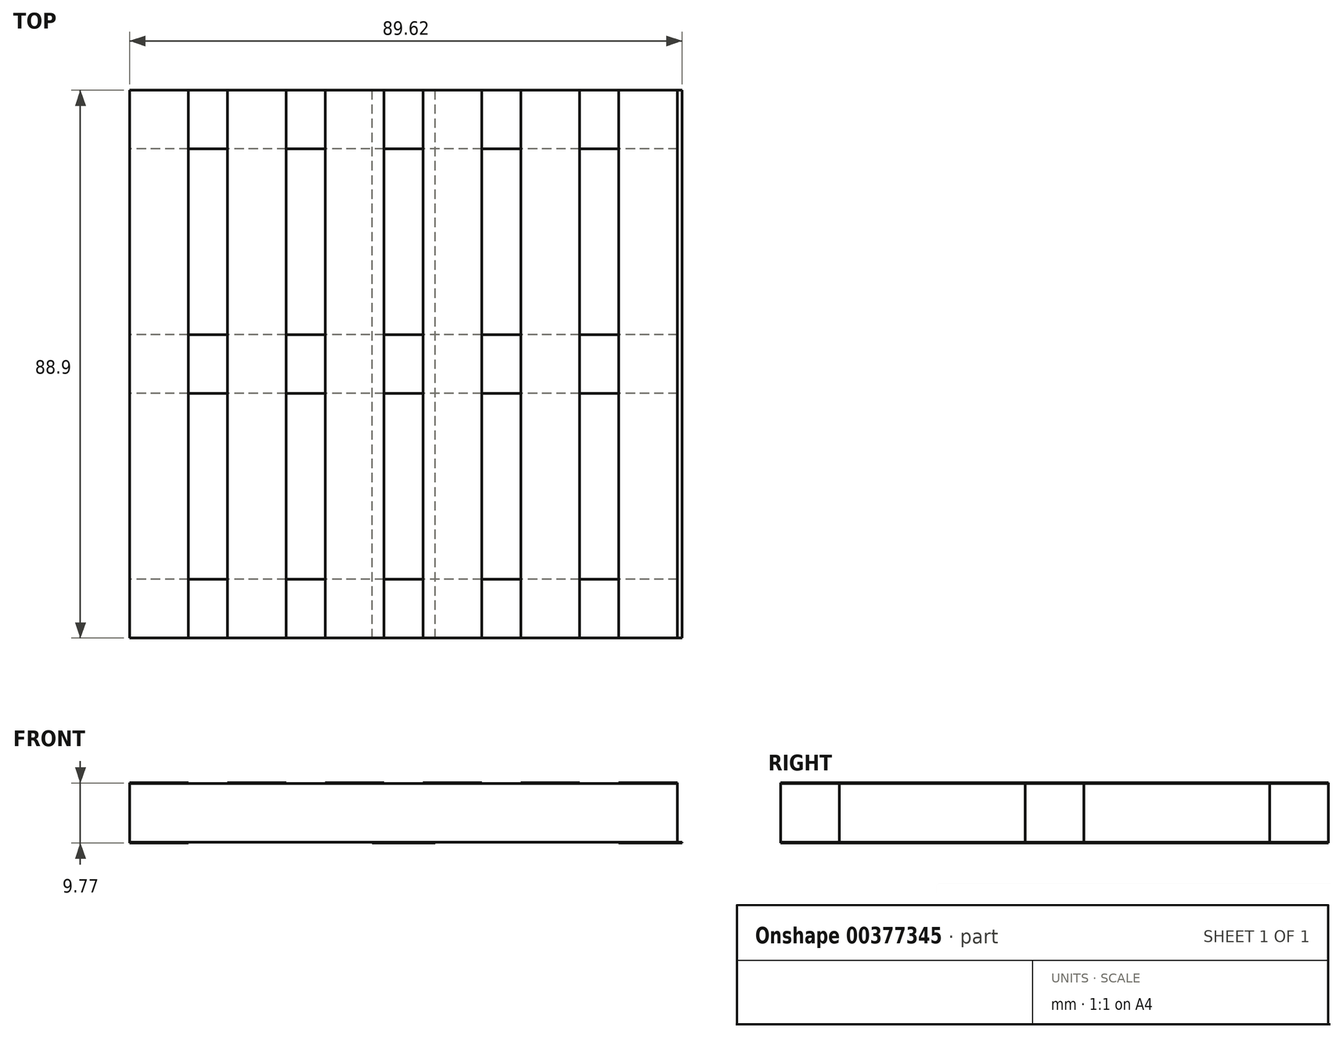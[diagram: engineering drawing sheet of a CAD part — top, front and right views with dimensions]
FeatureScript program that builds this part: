
annotation { "Feature Type Name" : "Feature", "Feature Type Description" : "" }
export const myFeature = defineFeature(function(context is Context, id is Id, definition is map)
    precondition{}
    {
        {
            assignVariable(context, id + "F0", {"name" : "slat_thickness", "anyValue" : 1 / 8});
        }
        {
            var Q0;
            Q0=qCreatedBy(makeId("Top.planeOp"),FACE);
            var sketch = newSketch(context, id + "F1", { "sketchPlane" : qUnion([Q0])});
            skLineSegment(sketch, "E0.bottom", {"start": v(44.45, -44.45) * mm, "end": v(-44.45, -44.45) * mm, "construction": true});
            skLineSegment(sketch, "E0.top", {"start": v(44.45, 44.45) * mm, "end": v(-44.45, 44.45) * mm, "construction": true});
            skLineSegment(sketch, "E0.left", {"start": v(44.45, -44.45) * mm, "end": v(44.45, 44.45) * mm, "construction": true});
            skLineSegment(sketch, "E0.right", {"start": v(-44.45, -44.45) * mm, "end": v(-44.45, 44.45) * mm, "construction": true});
            skPoint(sketch, "E0.middle", {"position": v(0, 0) * mm});
            skLineSegment(sketch, "E1.bottom", {"start": v(-44.45, -44.45) * mm, "end": v(-34.92, -44.45) * mm});
            skLineSegment(sketch, "E1.top", {"start": v(-44.45, 44.45) * mm, "end": v(-34.93, 44.45) * mm});
            skLineSegment(sketch, "E1.left", {"start": v(-44.45, -44.45) * mm, "end": v(-44.45, 44.45) * mm});
            skLineSegment(sketch, "E1.right", {"start": v(-34.92, -44.45) * mm, "end": v(-34.93, 44.45) * mm});
            skLineSegment(sketch, "E2.1.0.0", {"start": v(-19.05, -44.45) * mm, "end": v(-19.05, 44.45) * mm});
            skLineSegment(sketch, "E2.1.0.1", {"start": v(-28.57, -44.45) * mm, "end": v(-28.58, 44.45) * mm});
            skLineSegment(sketch, "E2.1.0.2", {"start": v(-28.58, 44.45) * mm, "end": v(-19.05, 44.45) * mm});
            skLineSegment(sketch, "E2.1.0.3", {"start": v(-28.57, -44.45) * mm, "end": v(-19.05, -44.45) * mm});
            skLineSegment(sketch, "E2.1.0.4", {"start": v(-28.57, -44.45) * mm, "end": v(-28.58, 44.45) * mm, "construction": true});
            skLineSegment(sketch, "E2.2.0.0", {"start": v(-3.17, -44.45) * mm, "end": v(-3.18, 44.45) * mm});
            skLineSegment(sketch, "E2.2.0.1", {"start": v(-12.7, -44.45) * mm, "end": v(-12.7, 44.45) * mm});
            skLineSegment(sketch, "E2.2.0.2", {"start": v(-12.7, 44.45) * mm, "end": v(-3.18, 44.45) * mm});
            skLineSegment(sketch, "E2.2.0.3", {"start": v(-12.7, -44.45) * mm, "end": v(-3.17, -44.45) * mm});
            skLineSegment(sketch, "E2.2.0.4", {"start": v(-12.7, -44.45) * mm, "end": v(-12.7, 44.45) * mm, "construction": true});
            skLineSegment(sketch, "E2.3.0.0", {"start": v(12.7, -44.45) * mm, "end": v(12.7, 44.45) * mm});
            skLineSegment(sketch, "E2.3.0.1", {"start": v(3.18, -44.45) * mm, "end": v(3.17, 44.45) * mm});
            skLineSegment(sketch, "E2.3.0.2", {"start": v(3.17, 44.45) * mm, "end": v(12.7, 44.45) * mm});
            skLineSegment(sketch, "E2.3.0.3", {"start": v(3.18, -44.45) * mm, "end": v(12.7, -44.45) * mm});
            skLineSegment(sketch, "E2.3.0.4", {"start": v(3.18, -44.45) * mm, "end": v(3.17, 44.45) * mm, "construction": true});
            skLineSegment(sketch, "E2.4.0.0", {"start": v(28.58, -44.45) * mm, "end": v(28.57, 44.45) * mm});
            skLineSegment(sketch, "E2.4.0.1", {"start": v(19.05, -44.45) * mm, "end": v(19.05, 44.45) * mm});
            skLineSegment(sketch, "E2.4.0.2", {"start": v(19.05, 44.45) * mm, "end": v(28.57, 44.45) * mm});
            skLineSegment(sketch, "E2.4.0.3", {"start": v(19.05, -44.45) * mm, "end": v(28.58, -44.45) * mm});
            skLineSegment(sketch, "E2.4.0.4", {"start": v(19.05, -44.45) * mm, "end": v(19.05, 44.45) * mm, "construction": true});
            skLineSegment(sketch, "E2.5.0.0", {"start": v(44.45, -44.45) * mm, "end": v(44.45, 44.45) * mm});
            skLineSegment(sketch, "E2.5.0.1", {"start": v(34.93, -44.45) * mm, "end": v(34.92, 44.45) * mm});
            skLineSegment(sketch, "E2.5.0.2", {"start": v(34.92, 44.45) * mm, "end": v(44.45, 44.45) * mm});
            skLineSegment(sketch, "E2.5.0.3", {"start": v(34.93, -44.45) * mm, "end": v(44.45, -44.45) * mm});
            skLineSegment(sketch, "E2.5.0.4", {"start": v(34.93, -44.45) * mm, "end": v(34.92, 44.45) * mm, "construction": true});
            skLineSegment(sketch, "E2.direction1", {"start": v(-44.45, -44.45) * mm, "end": v(-28.57, -44.45) * mm, "construction": true});
            skSolve(sketch);
        }
        {
            var Q0;
            Q0 = qSketchRegion(id + "F1", true);
            extrude(context, id + "F2", {"entities" : qUnion([Q0]), "depth" : (getVariable(context, 'slat_thickness')) * mm});
        }
        {
            var Q0;
            Q0=qCreatedBy(makeId("Right.planeOp"),FACE);
            var sketch = newSketch(context, id + "F3", { "sketchPlane" : qUnion([Q0])});
            skLineSegment(sketch, "E3.bottom", {"start": v(-44.45, 0) * mm, "end": v(-34.92, 0) * mm});
            skLineSegment(sketch, "E3.top", {"start": v(-44.45, -9.52) * mm, "end": v(-34.92, -9.52) * mm});
            skLineSegment(sketch, "E3.left", {"start": v(-44.45, 0) * mm, "end": v(-44.45, -9.53) * mm});
            skLineSegment(sketch, "E3.right", {"start": v(-34.92, 0) * mm, "end": v(-34.92, -9.53) * mm});
            skLineSegment(sketch, "E4.bottom", {"start": v(44.45, 0) * mm, "end": v(34.93, 0) * mm});
            skLineSegment(sketch, "E4.top", {"start": v(44.45, -9.52) * mm, "end": v(34.93, -9.53) * mm});
            skLineSegment(sketch, "E4.left", {"start": v(44.45, 0) * mm, "end": v(44.45, -9.53) * mm});
            skLineSegment(sketch, "E4.right", {"start": v(34.93, 0) * mm, "end": v(34.93, -9.53) * mm});
            skLineSegment(sketch, "E5.bottom", {"start": v(-4.76, 0) * mm, "end": v(4.76, 0) * mm});
            skLineSegment(sketch, "E5.top", {"start": v(-4.76, -9.52) * mm, "end": v(4.76, -9.52) * mm});
            skLineSegment(sketch, "E5.left", {"start": v(-4.76, 0) * mm, "end": v(-4.76, -9.52) * mm});
            skLineSegment(sketch, "E5.right", {"start": v(4.76, 0) * mm, "end": v(4.76, -9.52) * mm});
            skSolve(sketch);
        }
        {
            var Q0;
            Q0 = qSketchRegion(id + "F3", true);
            var Q1;
            Q1=makeQuery(id+"F2.opExtrude","SWEPT_FACE",FACE,{"disambiguationData":[OSD([sQuery(id+"F1.wireOp",EDGE,"E2.5.0.0")])]});
            var Q2;
            Q2=makeQuery(id+"F2.opExtrude","SWEPT_FACE",FACE,{"disambiguationData":[OSD([sQuery(id+"F1.wireOp",EDGE,"E1.left")])]});
            extrude(context, id + "F4", {"entities" : qUnion([Q0]), "endBound" : BoundingType.UP_TO_SURFACE, "endBoundEntityFace" : qUnion([Q1]), "depth" : 25.4 * mm, "hasSecondDirection" : true, "secondDirectionBound" : SecondDirectionBoundingType.UP_TO_SURFACE, "secondDirectionOppositeDirection" : true, "secondDirectionBoundEntityFace" : qUnion([Q2]), "secondDirectionDepth" : 25.4 * mm});
        }
        {
            var Q0;
            Q0=makeQuery(id+"F4.opExtrude","SWEPT_FACE",FACE,{"disambiguationData":[OSD([sQuery(id+"F3.wireOp",EDGE,"E5.top")])]});
            var sketch = newSketch(context, id + "F5", { "sketchPlane" : qUnion([Q0])});
            skLineSegment(sketch, "E6.bottom", {"start": v(45.17, 44.45) * mm, "end": v(34.92, 44.45) * mm});
            skLineSegment(sketch, "E6.top", {"start": v(45.17, -44.45) * mm, "end": v(34.93, -44.45) * mm});
            skLineSegment(sketch, "E6.left", {"start": v(45.17, 44.45) * mm, "end": v(45.17, -44.45) * mm});
            skLineSegment(sketch, "E6.right", {"start": v(34.92, 44.45) * mm, "end": v(34.93, -44.45) * mm});
            skLineSegment(sketch, "E7.bottom", {"start": v(-34.93, 44.45) * mm, "end": v(-44.45, 44.45) * mm});
            skLineSegment(sketch, "E7.top", {"start": v(-34.92, -44.45) * mm, "end": v(-44.45, -44.45) * mm});
            skLineSegment(sketch, "E7.left", {"start": v(-34.93, 44.45) * mm, "end": v(-34.92, -44.45) * mm});
            skLineSegment(sketch, "E7.right", {"start": v(-44.45, 44.45) * mm, "end": v(-44.45, -44.45) * mm});
            skLineSegment(sketch, "E8.bottom", {"start": v(-5.12, 44.45) * mm, "end": v(5.12, 44.45) * mm});
            skLineSegment(sketch, "E8.top", {"start": v(-5.12, -44.45) * mm, "end": v(5.12, -44.45) * mm});
            skLineSegment(sketch, "E8.left", {"start": v(-5.12, 44.45) * mm, "end": v(-5.12, -44.45) * mm});
            skLineSegment(sketch, "E8.right", {"start": v(5.12, 44.45) * mm, "end": v(5.12, -44.45) * mm});
            skLineSegment(sketch, "E9", {"start": v(5.12, 0) * mm, "end": v(-5.12, 0) * mm, "construction": true});
            skSolve(sketch);
        }
        {
            var Q0;
            Q0 = qSketchRegion(id + "F5", true);
            extrude(context, id + "F6", {"entities" : qUnion([Q0]), "depth" : (getVariable(context, 'slat_thickness')) * mm});
        }
    });
